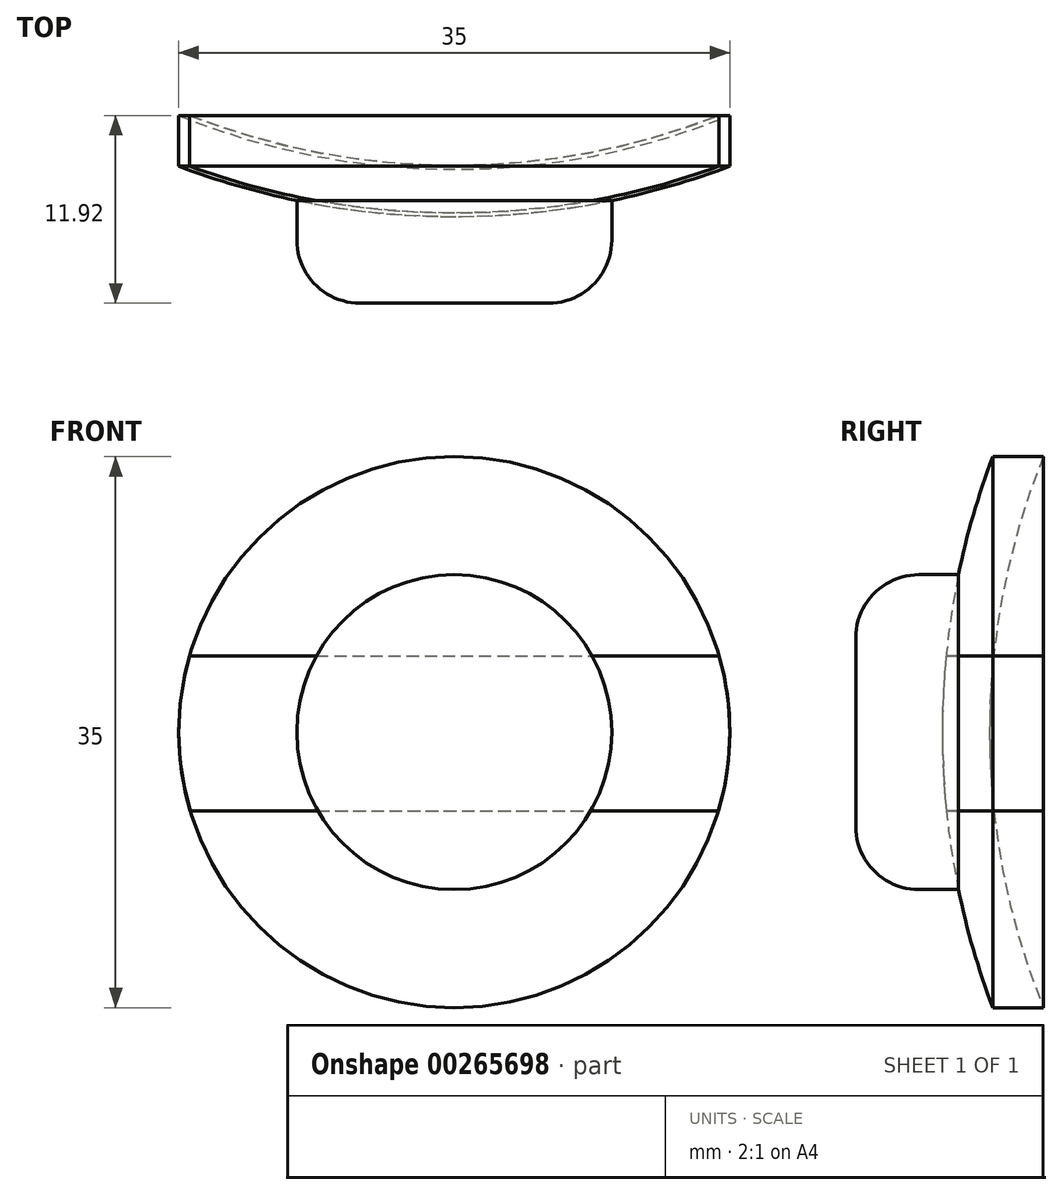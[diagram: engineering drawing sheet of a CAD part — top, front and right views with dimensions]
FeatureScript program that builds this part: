
annotation { "Feature Type Name" : "Feature", "Feature Type Description" : "" }
export const myFeature = defineFeature(function(context is Context, id is Id, definition is map)
    precondition{}
    {
        {
            var Q0;
            Q0=qCreatedBy(makeId("Front.planeOp"),FACE);
            var sketch = newSketch(context, id + "F0", { "sketchPlane" : qUnion([Q0])});
            skArc(sketch, "E0", {"start": v(0, -50) * mm, "mid": v(50, 0) * mm, "end": v(0, 50) * mm});
            skLineSegment(sketch, "E1", {"start": v(0, 50) * mm, "end": v(0, -50) * mm});
            skLineSegment(sketch, "E2", {"start": v(0, 5) * mm, "end": v(49.75, 5) * mm});
            skLineSegment(sketch, "E3", {"start": v(0, -5) * mm, "end": v(49.75, -5) * mm});
            skSolve(sketch);
        }
        {
            var Q0;
            {var subQ3=sQuery(id+"F0.wireOp",EDGE,"E2");Q0=makeQuery(id+"F0.imprint","IMPRINT",FACE,{"disambiguationData":[TD([[makeQuery(id+"F0.imprint","IMPRINT",EDGE,{"derivedFrom":subQ3}),1.0]])]});}
            var Q1;
            {var subQ3=sQuery(id+"F0.wireOp",EDGE,"E3");Q1=makeQuery(id+"F0.imprint","IMPRINT",FACE,{"disambiguationData":[TD([[makeQuery(id+"F0.imprint","IMPRINT",EDGE,{"derivedFrom":subQ3}),-1.0]])]});}
            var Q2;
            Q2=sQuery(id+"F0.wireOp",EDGE,"E1");
            revolve(context, id + "F1", {"entities" : qUnion([Q0, Q1]), "axis" : qUnion([Q2]), "revolveType" : RevolveType.FULL});
        }
        {
            var Q0;
            Q0=makeQuery(id+"F1.opRevolve","SWEPT_FACE",FACE,{"disambiguationData":[OSD([sQuery(id+"F0.wireOp",EDGE,"E2")])]});
            var Q1;
            Q1=makeQuery(id+"F1.opRevolve","SWEPT_FACE",FACE,{"disambiguationData":[OSD([sQuery(id+"F0.wireOp",EDGE,"E3")])]});
            shell(context, id + "F2", {"entities" : qUnion([Q0, Q1]), "thickness" : 3 * mm});
        }
        {
            var Q0;
            Q0=qCreatedBy(makeId("Front.planeOp"),FACE);
            var sketch = newSketch(context, id + "F3", { "sketchPlane" : qUnion([Q0])});
            skCircle(sketch, "E4", {"center": v(0, 0) * mm, "radius": 17.5 * mm});
            skSolve(sketch);
        }
        {
            var Q0;
            Q0 = qSketchRegion(id + "F3", true);
            extrude(context, id + "F4", {"entities" : qUnion([Q0]), "operationType" : NewBodyOperationType.REMOVE, "endBound" : BoundingType.THROUGH_ALL, "depth" : 25 * mm});
        }
        {
            var Q0;
            Q0=qCreatedBy(makeId("Front.planeOp"),FACE);
            var sketch = newSketch(context, id + "F5", { "sketchPlane" : qUnion([Q0])});
            skCircle(sketch, "E5", {"center": v(0, 0) * mm, "radius": 49.5 * mm});
            skCircle(sketch, "E6.0", {"center": v(0, 0) * mm, "radius": 46.5 * mm});
            skLineSegment(sketch, "E7", {"start": v(0, 59.3) * mm, "end": v(0, -57.68) * mm, "construction": true});
            skLineSegment(sketch, "E8", {"start": v(0, 4.84) * mm, "end": v(49.26, 4.84) * mm});
            skLineSegment(sketch, "E9", {"start": v(0, -5) * mm, "end": v(49.25, -5) * mm});
            skSolve(sketch);
        }
        {
            var Q0;
            {var subQ0=sQuery(id+"F5.wireOp",EDGE,"E8");var subQ1=sQuery(id+"F5.wireOp",EDGE,"E5");var subQ2=makeQuery(id+"F5.imprint","INTERSECT",VERTEX,{"derivedFrom":[subQ1,subQ0]});Q0=makeQuery(id+"F5.imprint","IMPRINT",FACE,{"disambiguationData":[TD([[makeQuery(id+"F5.imprint","IMPRINT",EDGE,{"disambiguationData":[TD([[subQ2,1.0]])],"derivedFrom":subQ1}),1.0]])]});}
            var Q1;
            Q1=sQuery(id+"F5.wireOp",EDGE,"E7");
            revolve(context, id + "F6", {"operationType" : NewBodyOperationType.ADD, "entities" : qUnion([Q0]), "axis" : qUnion([Q1]), "revolveType" : RevolveType.FULL});
        }
        {
            var Q0;
            Q0=qCreatedBy(makeId("Front.planeOp"),FACE);
            var sketch = newSketch(context, id + "F7", { "sketchPlane" : qUnion([Q0])});
            skArc(sketch, "E10", {"start": v(0, -49.5) * mm, "mid": v(49.5, 0) * mm, "end": v(0, 49.5) * mm});
            skArc(sketch, "E11.0", {"start": v(0, -46.5) * mm, "mid": v(46.5, 0) * mm, "end": v(0, 46.5) * mm});
            skLineSegment(sketch, "E12", {"start": v(0, 49.5) * mm, "end": v(0, -49.5) * mm});
            skSolve(sketch);
        }
        {
            var Q0;
            {var subQ0=sQuery(id+"F7.wireOp",EDGE,"E10");Q0=makeQuery(id+"F7.imprint","IMPRINT",FACE,{"disambiguationData":[TD([[makeQuery(id+"F7.imprint","IMPRINT",EDGE,{"derivedFrom":subQ0}),1.0]])]});}
            var Q1;
            Q1=sQuery(id+"F7.wireOp",EDGE,"E12");
            revolve(context, id + "F8", {"entities" : qUnion([Q0]), "axis" : qUnion([Q1]), "revolveType" : RevolveType.FULL});
        }
        {
            var Q0;
            Q0=qCreatedBy(makeId("Front.planeOp"),FACE);
            var sketch = newSketch(context, id + "F9", { "sketchPlane" : qUnion([Q0])});
            skCircle(sketch, "E13", {"center": v(0, 0) * mm, "radius": 17.5 * mm});
            skSolve(sketch);
        }
        {
            var Q0;
            Q0 = qSketchRegion(id + "F9", true);
            extrude(context, id + "F10", {"entities" : qUnion([Q0]), "operationType" : NewBodyOperationType.INTERSECT, "endBound" : BoundingType.THROUGH_ALL, "depth" : 25 * mm});
        }
        {
            var Q0;
            Q0=qCreatedBy(makeId("Front.planeOp"),FACE);
            cPlane(context, id + "F11", {"entities" : qUnion([Q0]), "cplaneType" : CPlaneType.OFFSET, "offset" : 55 * mm, "width" : 150 * mm, "height" : 150 * mm});
        }
        {
            var Q0;
            Q0=qCreatedBy(id+"F11.planeOp",FACE);
            var sketch = newSketch(context, id + "F12", { "sketchPlane" : qUnion([Q0])});
            skCircle(sketch, "E14", {"center": v(0, 0) * mm, "radius": 10 * mm});
            skSolve(sketch);
        }
        {
            var Q0;
            Q0 = qSketchRegion(id + "F12", true);
            extrude(context, id + "F13", {"entities" : qUnion([Q0]), "endBound" : BoundingType.UP_TO_NEXT, "oppositeDirection" : true, "depth" : 25 * mm});
        }
        {
            var Q0;
            Q0=makeQuery(id+"F13.opExtrude","CAP_EDGE",EDGE,{"disambiguationData":[OSD([sQuery(id+"F12.wireOp",EDGE,"E14")])],"isStart":true});
            fillet(context, id + "F14", {"entities" : qUnion([Q0]), "radius" : 4 * mm, "tangentPropagation" : true, "allowEdgeOverflow" : false});
        }
    });
